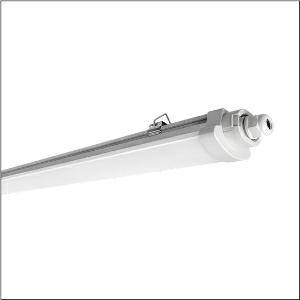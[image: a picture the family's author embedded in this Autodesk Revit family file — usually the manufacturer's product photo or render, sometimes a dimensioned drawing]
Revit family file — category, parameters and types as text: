
# Revit family: monsun_r__41_51fk20mk440a_a1bd
name_source: partatom
category: Lighting Fixtures
units: mm (PartAtom-declared; Revit-internal decimal feet)

## family parameters
Cut with Voids When Loaded = No
Host = Face
Light Source = No
Part Type = Normal
Room Calculation Point = No
Round Connector Dimension = Use Diameter
Shared = No

## types (1)
- --- (1 x LED, 4000 lm, 30 W, 4000K)
    Apparent Load = 30 VA
    CIE Flux Codes = 44 74 92 92 100
    Color Rendering = 80
    Color Temperature = 4000K
    Default Elevation = 1800 mm
    Description = Monsun® 41, damp-proof luminaire, primary optical cover: diffuser, of PC, frosted, light emission: direct distribution, primary light characteristic: symmetric, installation type: surface-mounted, suspended mounting, LED, rated luminous flux: 4.000lm, luminous efficacy: 130lm/W, light colour: 840, colour temperature: 4000K, control gear: ECG Multilumen, with terminal, 3-pole, mains connection: 220..240V, AC, 50/60Hz, rated input power: 30W, housing, luminaire housing, of PC, grey, length: 1.200mm, width: 79mm, height: 52mm, end cap, of PC, grey, ceiling mounting element, of stainless steel (V2A), protection rating (complete): IP65, insulation class (complete): insulation class II (safety insulation), certification: CE, UKCA, protection symbol: D, impact resistance: IK08, permissible operating ambient temperature: -20..+35°C, corresponds to IFS (International Featured Standards) requirements for safety and quality in the food industry, contact your sales advisor before using the luminaires in applications with unclear chemical exposure, large temperature fluctuations or condensation-forming humidity, packaging unit: 1 piece
    Height = 54 mm
    Lamp = 1 x LED
    Lamp Light Flux = 4000 lm
    Lamp Power = 30 W
    Lamp count = 1
    Length = 1200 mm
    Luminous efficacy = 133 lm/W
    Manufacturer = Siteco
    ModVariant = No
    Model = 51FK20MK440A
    Mounting Place = Ceiling
    Mounting Type = Surface mounted
    Number of Poles = 1
    OnlyDefault = Yes
    Power Factor = 1
    Product Name = Monsun® 41
    Product group = damp-proof luminaire
    ProductGroupID = 300
    Protection Class = Protection class II
    Protection Degree = IP 65
    RLX_Detail_Level = 1
    RLX_Emergency_Light_Flux = 0 lm
    RLX_Emergency_Type = 0
    RLX_Emergency_Type_DB = No
    RlxData = <blob elided: 31997 chars, md5=3c9310bc>
    Socket = socket
    Standby Power = 0 W
    System Light Flux = 4000 lm
    System Power = 30 W
    Type Comments = factory setting: luminous flux: 100 % | (HIGH)
    Type Image = l_1007037.jpg
    URL = http://relux.com
    VarID = @adj_145811
    Voltage = 0 V
    Weight = 0.00 kg
    Width = 79 mm

## geometry (parser evidence)
native form markers: Blend x4, Sweep x12
no freeform markers — native parametric forms only
